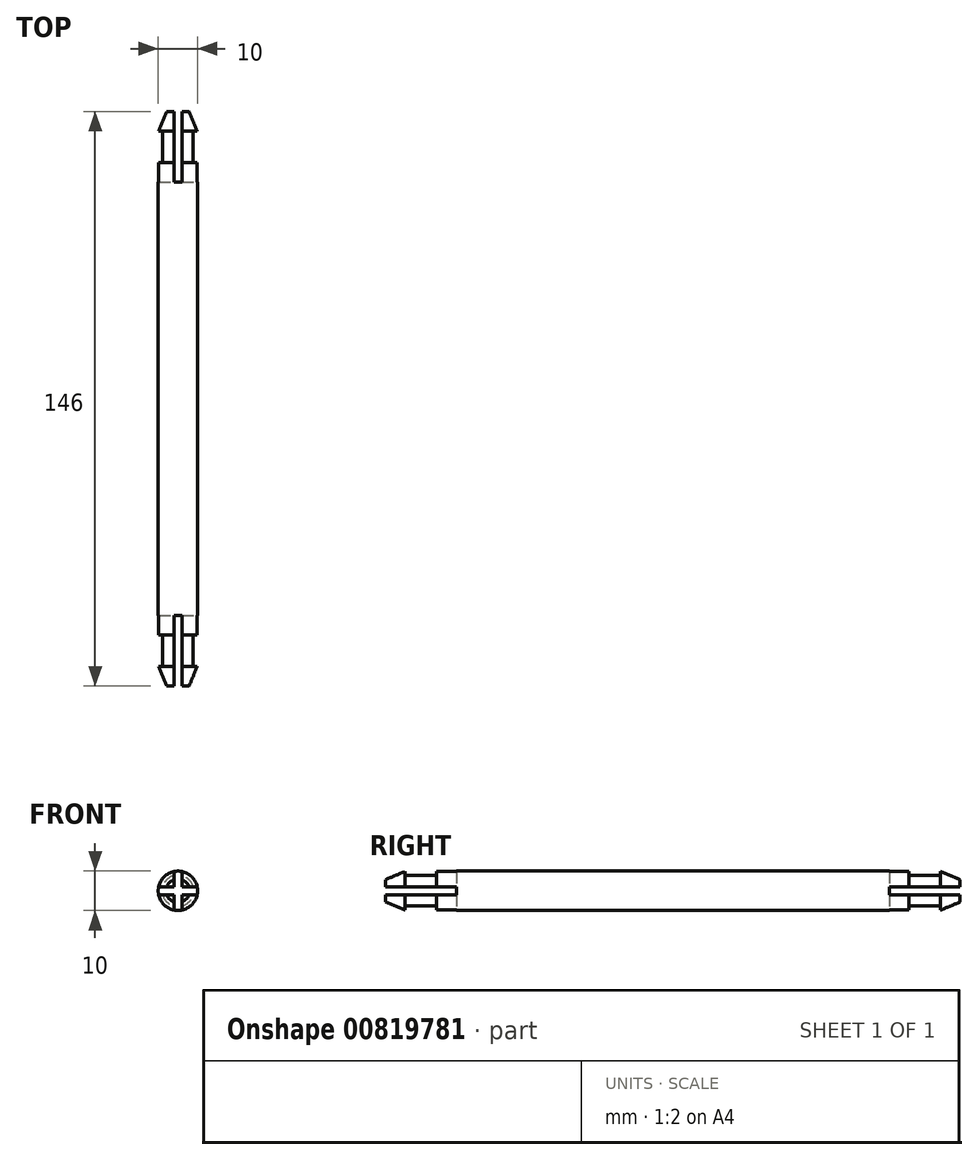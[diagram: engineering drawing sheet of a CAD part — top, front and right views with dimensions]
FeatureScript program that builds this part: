
annotation { "Feature Type Name" : "Feature", "Feature Type Description" : "" }
export const myFeature = defineFeature(function(context is Context, id is Id, definition is map)
    precondition{}
    {
        {
            var Q0;
            Q0=qCreatedBy(makeId("Top.planeOp"),FACE);
            var sketch = newSketch(context, id + "F0", { "sketchPlane" : qUnion([Q0])});
            skLineSegment(sketch, "E0", {"start": v(0, 0) * mm, "end": v(0, 60) * mm});
            skLineSegment(sketch, "E1.bottom", {"start": v(0, 60) * mm, "end": v(5, 60) * mm});
            skLineSegment(sketch, "E1.top", {"start": v(0, 0) * mm, "end": v(5, 0) * mm});
            skLineSegment(sketch, "E1.left", {"start": v(0, 60) * mm, "end": v(0, 0) * mm});
            skLineSegment(sketch, "E1.right", {"start": v(5, 60) * mm, "end": v(5, 0) * mm});
            skLineSegment(sketch, "E2.bottom", {"start": v(0, 60) * mm, "end": v(4, 60) * mm});
            skLineSegment(sketch, "E2.top", {"start": v(0, 68) * mm, "end": v(4, 68) * mm});
            skLineSegment(sketch, "E2.left", {"start": v(0, 60) * mm, "end": v(0, 68) * mm});
            skLineSegment(sketch, "E2.right", {"start": v(4, 60) * mm, "end": v(4, 68) * mm});
            skLineSegment(sketch, "E3", {"start": v(0, 68) * mm, "end": v(0, 73) * mm});
            skLineSegment(sketch, "E4", {"start": v(4, 68) * mm, "end": v(5, 68) * mm});
            skLineSegment(sketch, "E5", {"start": v(0, 73) * mm, "end": v(3, 73) * mm});
            skLineSegment(sketch, "E6", {"start": v(3, 73) * mm, "end": v(5, 68) * mm});
            skSolve(sketch);
        }
        {
            var Q0;
            Q0=makeQuery(id+"F0.imprint","IMPRINT",FACE,{"disambiguationData":[TD([[makeQuery(id+"F0.imprint","IMPRINT",EDGE,{"derivedFrom":sQuery(id+"F0.wireOp",EDGE,"E2.top")}),1.0]])]});
            var Q1;
            Q1=makeQuery(id+"F0.imprint","IMPRINT",FACE,{"disambiguationData":[TD([[makeQuery(id+"F0.imprint","IMPRINT",EDGE,{"derivedFrom":sQuery(id+"F0.wireOp",EDGE,"E2.top")}),-1.0]])]});
            var Q2;
            {var subQ3=sQuery(id+"F0.wireOp",EDGE,"E0");Q2=makeQuery(id+"F0.imprint","IMPRINT",FACE,{"disambiguationData":[TD([[makeQuery(id+"F0.imprint","IMPRINT",EDGE,{"derivedFrom":subQ3}),-1.0]])]});}
            var Q3;
            Q3=sQuery(id+"F0.wireOp",EDGE,"E1.left");
            revolve(context, id + "F1", {"surfaceOperationType" : NewSurfaceOperationType.NEW, "entities" : qUnion([Q0, Q1, Q2]), "axis" : qUnion([Q3]), "revolveType" : RevolveType.FULL});
        }
        {
            var Q0;
            Q0=qCreatedBy(makeId("Front.planeOp"),FACE);
            var sketch = newSketch(context, id + "F2", { "sketchPlane" : qUnion([Q0])});
            skLineSegment(sketch, "E7.bottom", {"start": v(-1, 11.15) * mm, "end": v(1, 11.15) * mm});
            skLineSegment(sketch, "E7.top", {"start": v(-1, -11.15) * mm, "end": v(1, -11.15) * mm});
            skLineSegment(sketch, "E7.left", {"start": v(-1, 11.15) * mm, "end": v(-1, -11.15) * mm});
            skLineSegment(sketch, "E7.right", {"start": v(1, 11.15) * mm, "end": v(1, -11.15) * mm});
            skLineSegment(sketch, "E8.bottom", {"start": v(-11.68, 1) * mm, "end": v(11.68, 1) * mm});
            skLineSegment(sketch, "E8.top", {"start": v(-11.68, -1) * mm, "end": v(11.68, -1) * mm});
            skLineSegment(sketch, "E8.left", {"start": v(-11.68, 1) * mm, "end": v(-11.68, -1) * mm});
            skLineSegment(sketch, "E8.right", {"start": v(11.68, 1) * mm, "end": v(11.68, -1) * mm});
            skLineSegment(sketch, "E9", {"start": v(-11.68, 1) * mm, "end": v(11.68, -1) * mm, "construction": true});
            skLineSegment(sketch, "E10", {"start": v(11.68, 1) * mm, "end": v(-11.68, -1) * mm, "construction": true});
            skLineSegment(sketch, "E11", {"start": v(-1, 11.15) * mm, "end": v(1, -11.15) * mm, "construction": true});
            skLineSegment(sketch, "E12", {"start": v(1, 11.15) * mm, "end": v(-1, -11.15) * mm, "construction": true});
            skPoint(sketch, "E13", {"position": v(0, 0) * mm});
            skSolve(sketch);
        }
        {
            var Q0;
            {var subQ5=sQuery(id+"F2.wireOp",EDGE,"E8.left");Q0=makeQuery(id+"F2.imprint","IMPRINT",FACE,{"disambiguationData":[TD([[makeQuery(id+"F2.imprint","IMPRINT",EDGE,{"derivedFrom":subQ5}),1.0]])]});}
            var Q1;
            {var subQ0=sQuery(id+"F2.wireOp",EDGE,"E8.bottom");var subQ1=sQuery(id+"F2.wireOp",EDGE,"E7.left");var subQ2=makeQuery(id+"F2.imprint","INTERSECT",VERTEX,{"derivedFrom":[subQ1,subQ0]});Q1=makeQuery(id+"F2.imprint","IMPRINT",FACE,{"disambiguationData":[TD([[makeQuery(id+"F2.imprint","IMPRINT",EDGE,{"disambiguationData":[TD([[subQ2,-1.0]])],"derivedFrom":subQ1}),1.0]])]});}
            var Q2;
            {var subQ0=sQuery(id+"F2.wireOp",EDGE,"E7.bottom");Q2=makeQuery(id+"F2.imprint","IMPRINT",FACE,{"disambiguationData":[TD([[makeQuery(id+"F2.imprint","IMPRINT",EDGE,{"derivedFrom":subQ0}),-1.0]])]});}
            var Q3;
            {var subQ5=sQuery(id+"F2.wireOp",EDGE,"E8.right");Q3=makeQuery(id+"F2.imprint","IMPRINT",FACE,{"disambiguationData":[TD([[makeQuery(id+"F2.imprint","IMPRINT",EDGE,{"derivedFrom":subQ5}),-1.0]])]});}
            var Q4;
            {var subQ0=sQuery(id+"F2.wireOp",EDGE,"E7.top");Q4=makeQuery(id+"F2.imprint","IMPRINT",FACE,{"disambiguationData":[TD([[makeQuery(id+"F2.imprint","IMPRINT",EDGE,{"derivedFrom":subQ0}),1.0]])]});}
            extrude(context, id + "F3", {"entities" : qUnion([Q0, Q1, Q2, Q3, Q4]), "operationType" : NewBodyOperationType.REMOVE, "oppositeDirection" : true, "depth" : 73 * mm, "offsetDistance" : 25 * mm, "hasSecondDirection" : true, "secondDirectionOppositeDirection" : true, "secondDirectionDepth" : 55 * mm});
        }
        {
            var Q0;
            Q0=makeQuery(id+"F1.opRevolve","SWEPT_BODY",BODY,{"disambiguationData":[OSD([sQuery(id+"F0.wireOp",EDGE,"E0"),sQuery(id+"F0.wireOp",EDGE,"E1.bottom"),sQuery(id+"F0.wireOp",EDGE,"E1.top"),sQuery(id+"F0.wireOp",EDGE,"E1.right"),sQuery(id+"F0.wireOp",EDGE,"E2.left"),sQuery(id+"F0.wireOp",EDGE,"E2.right"),sQuery(id+"F0.wireOp",EDGE,"E3"),sQuery(id+"F0.wireOp",EDGE,"E4"),sQuery(id+"F0.wireOp",EDGE,"E5"),sQuery(id+"F0.wireOp",EDGE,"E6")])]});
            var Q1;
            Q1=makeQuery(id+"F1.opRevolve","SWEPT_FACE",FACE,{"disambiguationData":[OSD([sQuery(id+"F0.wireOp",EDGE,"E1.top")])]});
            mirror(context, id + "F4", {"operationType" : NewBodyOperationType.ADD, "entities" : qUnion([Q0]), "mirrorPlane" : qUnion([Q1])});
        }
    });
